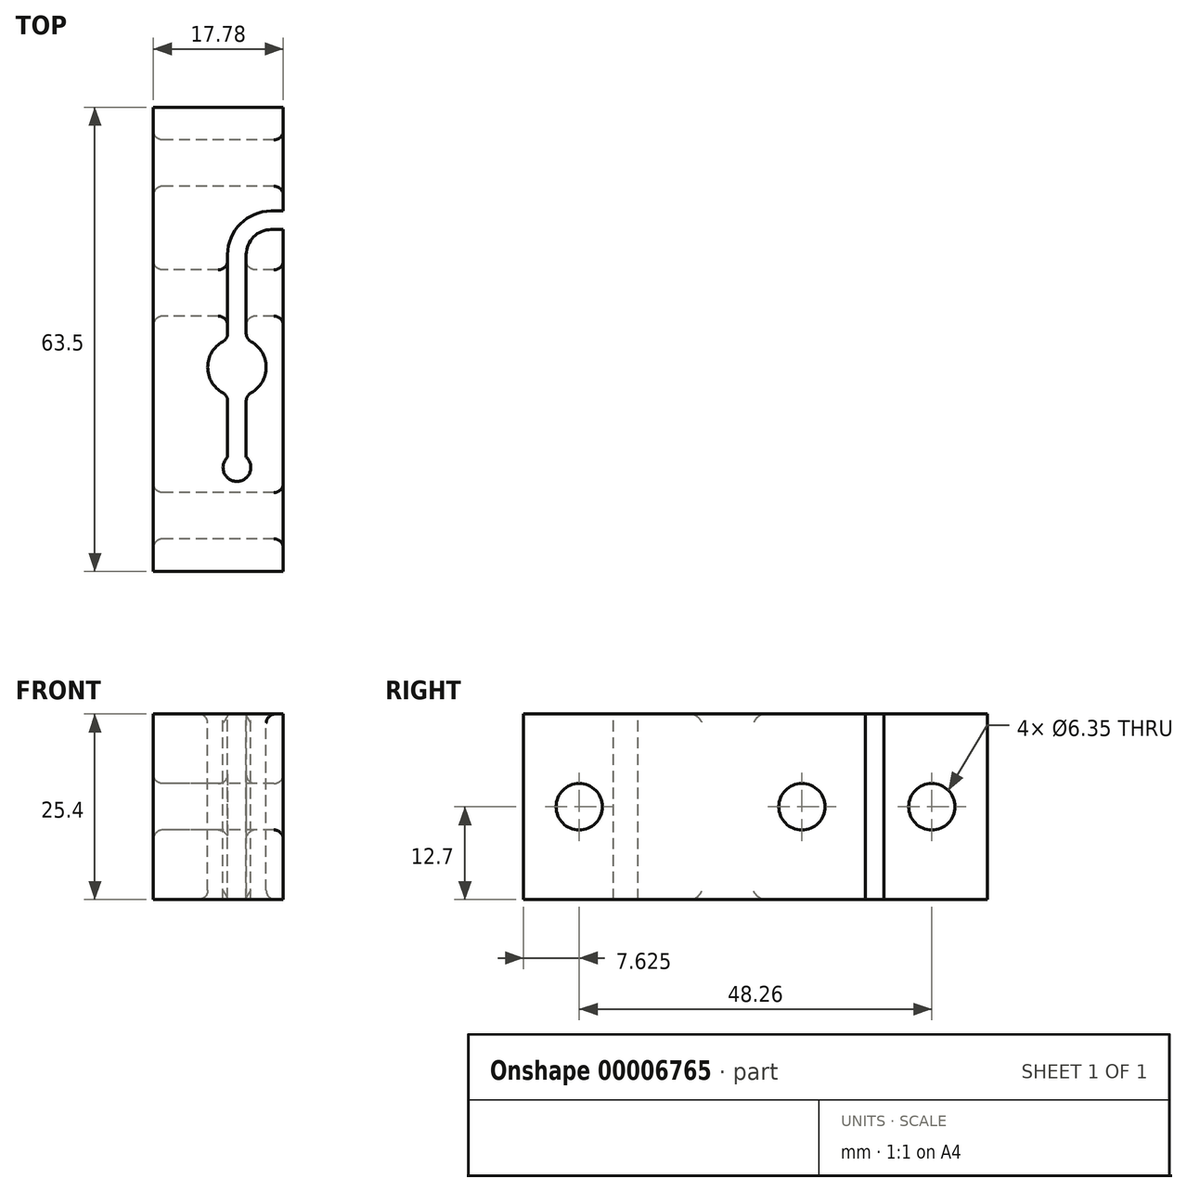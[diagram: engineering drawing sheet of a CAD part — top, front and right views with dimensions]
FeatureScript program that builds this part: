
annotation { "Feature Type Name" : "Feature", "Feature Type Description" : "" }
export const myFeature = defineFeature(function(context is Context, id is Id, definition is map)
    precondition{}
    {
        {
            var Q0;
            Q0=qCreatedBy(makeId("Top.planeOp"),FACE);
            var sketch = newSketch(context, id + "F0", { "sketchPlane" : qUnion([Q0])});
            skLineSegment(sketch, "E0", {"start": v(-46.47, 46.77) * mm, "end": v(-46.47, -16.73) * mm});
            skLineSegment(sketch, "E1", {"start": v(-46.47, -16.73) * mm, "end": v(-28.69, -16.73) * mm});
            skLineSegment(sketch, "E2", {"start": v(-28.69, -16.73) * mm, "end": v(-28.69, 46.77) * mm});
            skLineSegment(sketch, "E3", {"start": v(-28.69, 46.77) * mm, "end": v(-46.47, 46.77) * mm});
            skSolve(sketch);
        }
        {
            var Q0;
            Q0=makeQuery(id+"F0.imprint","IMPRINT",FACE,{"disambiguationData":[TD([[makeQuery(id+"F0.imprint","IMPRINT",EDGE,{"derivedFrom":sQuery(id+"F0.wireOp",EDGE,"E0")}),1.0]])]});
            extrude(context, id + "F1", {"entities" : qUnion([Q0]), "depth" : 25.4 * mm});
        }
        {
            var Q0;
            Q0=makeQuery(id+"F1.opExtrude","SWEPT_FACE",FACE,{"disambiguationData":[OSD([sQuery(id+"F0.wireOp",EDGE,"E0")])]});
            var sketch = newSketch(context, id + "F2", { "sketchPlane" : qUnion([Q0])});
            skCircle(sketch, "E4", {"center": v(-39.15, 12.7) * mm, "radius": 3.18 * mm});
            skCircle(sketch, "E5", {"center": v(9.1, 12.7) * mm, "radius": 3.18 * mm});
            skCircle(sketch, "E6", {"center": v(-21.37, 12.7) * mm, "radius": 3.18 * mm});
            skSolve(sketch);
        }
        {
            var Q0;
            Q0=makeQuery(id+"F2.imprint","IMPRINT",FACE,{"disambiguationData":[TD([[makeQuery(id+"F2.imprint","IMPRINT",EDGE,{"derivedFrom":sQuery(id+"F2.wireOp",EDGE,"E4")}),1.0]])]});
            var Q1;
            Q1=makeQuery(id+"F2.imprint","IMPRINT",FACE,{"disambiguationData":[TD([[makeQuery(id+"F2.imprint","IMPRINT",EDGE,{"derivedFrom":sQuery(id+"F2.wireOp",EDGE,"E6")}),1.0]])]});
            var Q2;
            Q2=makeQuery(id+"F2.imprint","IMPRINT",FACE,{"disambiguationData":[TD([[makeQuery(id+"F2.imprint","IMPRINT",EDGE,{"derivedFrom":sQuery(id+"F2.wireOp",EDGE,"E5")}),1.0]])]});
            extrude(context, id + "F3", {"entities" : qUnion([Q0, Q1, Q2]), "operationType" : NewBodyOperationType.REMOVE, "endBound" : BoundingType.THROUGH_ALL, "oppositeDirection" : true, "depth" : 25.4 * mm});
        }
        {
            var Q0;
            Q0=makeQuery(id+"F1.opExtrude","CAP_FACE",FACE,{"disambiguationData":[OSD([sQuery(id+"F0.wireOp",EDGE,"E0"),sQuery(id+"F0.wireOp",EDGE,"E1"),sQuery(id+"F0.wireOp",EDGE,"E2"),sQuery(id+"F0.wireOp",EDGE,"E3")])],"isStart":false});
            var sketch = newSketch(context, id + "F4", { "sketchPlane" : qUnion([Q0])});
            skCircle(sketch, "E7", {"center": v(-35.04, 11.21) * mm, "radius": 4 * mm});
            skLineSegment(sketch, "E8", {"start": v(-28.69, 30.05) * mm, "end": v(-30.34, 30.05) * mm});
            skArc(sketch, "E9", {"start": v(-30.34, 30.05) * mm, "mid": v(-32.76, 29.05) * mm, "end": v(-33.77, 26.63) * mm});
            skLineSegment(sketch, "E10", {"start": v(-33.77, 26.63) * mm, "end": v(-33.77, 15) * mm});
            skLineSegment(sketch, "E11.0", {"start": v(-36.3, 26.63) * mm, "end": v(-36.3, 15) * mm});
            skArc(sketch, "E11.1", {"start": v(-30.34, 32.6) * mm, "mid": v(-34.56, 30.84) * mm, "end": v(-36.3, 26.63) * mm});
            skLineSegment(sketch, "E11.2", {"start": v(-28.69, 32.6) * mm, "end": v(-30.34, 32.6) * mm});
            skLineSegment(sketch, "E12", {"start": v(-36.3, 7.42) * mm, "end": v(-36.3, -1.08) * mm});
            skLineSegment(sketch, "E13", {"start": v(-33.77, 7.42) * mm, "end": v(-33.77, -1.08) * mm});
            skCircle(sketch, "E14", {"center": v(-35.04, -2.5) * mm, "radius": 1.9 * mm});
            skSolve(sketch);
        }
        {
            var Q0;
            {var subQ4=sQuery(id+"F4.wireOp",EDGE,"E8");Q0=makeQuery(id+"F4.imprint","IMPRINT",FACE,{"disambiguationData":[TD([[makeQuery(id+"F4.imprint","IMPRINT",EDGE,{"derivedFrom":subQ4}),-1.0]])]});}
            var Q1;
            {var subQ0=sQuery(id+"F4.wireOp",EDGE,"E7");var subQ2=makeQuery(id+"F4.imprint","INTERSECT",VERTEX,{"derivedFrom":[subQ0,sQuery(id+"F4.wireOp",EDGE,"E10")]});Q1=makeQuery(id+"F4.imprint","IMPRINT",FACE,{"disambiguationData":[TD([[makeQuery(id+"F4.imprint","IMPRINT",EDGE,{"disambiguationData":[TD([[subQ2,-1.0]])],"derivedFrom":subQ0}),1.0]])]});}
            var Q2;
            {var subQ1=sQuery(id+"F4.wireOp",EDGE,"E12");Q2=makeQuery(id+"F4.imprint","IMPRINT",FACE,{"disambiguationData":[TD([[makeQuery(id+"F4.imprint","IMPRINT",EDGE,{"derivedFrom":subQ1}),1.0]])]});}
            var Q3;
            {var subQ0=sQuery(id+"F4.wireOp",EDGE,"E14");var subQ2=makeQuery(id+"F4.imprint","INTERSECT",VERTEX,{"derivedFrom":[sQuery(id+"F4.wireOp",EDGE,"E12"),subQ0]});Q3=makeQuery(id+"F4.imprint","IMPRINT",FACE,{"disambiguationData":[TD([[makeQuery(id+"F4.imprint","IMPRINT",EDGE,{"disambiguationData":[TD([[subQ2,1.0]])],"derivedFrom":subQ0}),1.0]])]});}
            extrude(context, id + "F5", {"entities" : qUnion([Q0, Q1, Q2, Q3]), "operationType" : NewBodyOperationType.REMOVE, "endBound" : BoundingType.THROUGH_ALL, "oppositeDirection" : true, "depth" : 25.4 * mm});
        }
        {
            var Q0;
            Q0=makeQuery(id+"F5.boolean.opBoolean","COPY",FACE,{"derivedFrom":makeQuery(id+"F5.opExtrude","SWEPT_FACE",FACE,{"disambiguationData":[OSD([sQuery(id+"F4.wireOp",EDGE,"E7")])]})});
            var Q1;
            Q1=makeQuery(id+"F3.boolean.opBoolean","COPY",FACE,{"derivedFrom":makeQuery(id+"F3.opExtrude","SWEPT_FACE",FACE,{"disambiguationData":[OSD([sQuery(id+"F2.wireOp",EDGE,"E5")])]})});
            var Q2;
            Q2=makeQuery(id+"F5.boolean.opBoolean","SPLIT",FACE,{"disambiguationData":[TD([makeQuery(id+"F1.opExtrude","SWEPT_FACE",FACE,{"disambiguationData":[OSD([sQuery(id+"F0.wireOp",EDGE,"E2")])]})])],"derivedFrom":makeQuery(id+"F3.boolean.opBoolean","COPY",FACE,{"derivedFrom":makeQuery(id+"F3.opExtrude","SWEPT_FACE",FACE,{"disambiguationData":[OSD([sQuery(id+"F2.wireOp",EDGE,"E6")])]})})});
            var Q3;
            Q3=makeQuery(id+"F3.boolean.opBoolean","COPY",FACE,{"derivedFrom":makeQuery(id+"F3.opExtrude","SWEPT_FACE",FACE,{"disambiguationData":[OSD([sQuery(id+"F2.wireOp",EDGE,"E4")])]})});
            var Q4;
            Q4=makeQuery(id+"F5.boolean.opBoolean","SPLIT",FACE,{"disambiguationData":[TD([makeQuery(id+"F1.opExtrude","SWEPT_FACE",FACE,{"disambiguationData":[OSD([sQuery(id+"F0.wireOp",EDGE,"E0")])]})])],"derivedFrom":makeQuery(id+"F3.boolean.opBoolean","COPY",FACE,{"derivedFrom":makeQuery(id+"F3.opExtrude","SWEPT_FACE",FACE,{"disambiguationData":[OSD([sQuery(id+"F2.wireOp",EDGE,"E6")])]})})});
            fillet(context, id + "F6", {"entities" : qUnion([Q0, Q1, Q2, Q3, Q4]), "radius" : 1.27 * mm, "tangentPropagation" : true, "allowEdgeOverflow" : false});
        }
    });
